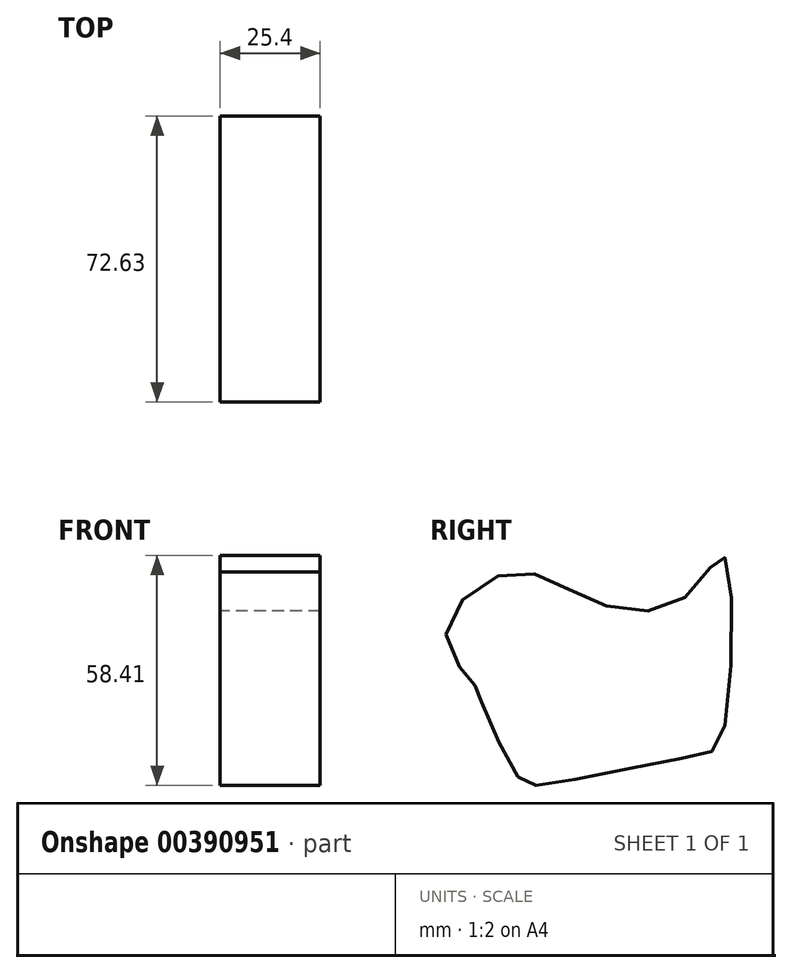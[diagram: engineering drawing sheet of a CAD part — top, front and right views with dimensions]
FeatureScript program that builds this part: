
annotation { "Feature Type Name" : "Feature", "Feature Type Description" : "" }
export const myFeature = defineFeature(function(context is Context, id is Id, definition is map)
    precondition{}
    {
        {
            var Q0;
            Q0=qCreatedBy(makeId("Right.planeOp"),FACE);
            var sketch = newSketch(context, id + "F0", { "sketchPlane" : qUnion([Q0])});
            skFitSpline(sketch, "E0", {"points": [v(-54.52, 18.66) * mm, v(-37.93, 34.39) * mm, v(-17.2, 27.13) * mm, v(6.83, 28.51) * mm, v(15.98, 38.54) * mm, v(15.81, -6.57) * mm, v(8.04, -12.27) * mm, v(-30.33, -19.53) * mm, v(-36.55, -17.1) * mm, v(-46.74, 4.5) * mm, v(-47.44, 6.05) * mm, v(-54.52, 18.66) * mm]});
            skSolve(sketch);
        }
        {
            var Q0;
            Q0=makeQuery(id+"F0.imprint","IMPRINT",FACE,{"disambiguationData":[TD([[makeQuery(id+"F0.imprint","IMPRINT",EDGE,{"derivedFrom":sQuery(id+"F0.wireOp",EDGE,"E0")}),-1.0]])]});
            extrude(context, id + "F1", {"entities" : qUnion([Q0]), "depth" : 25.4 * mm});
        }
    });
